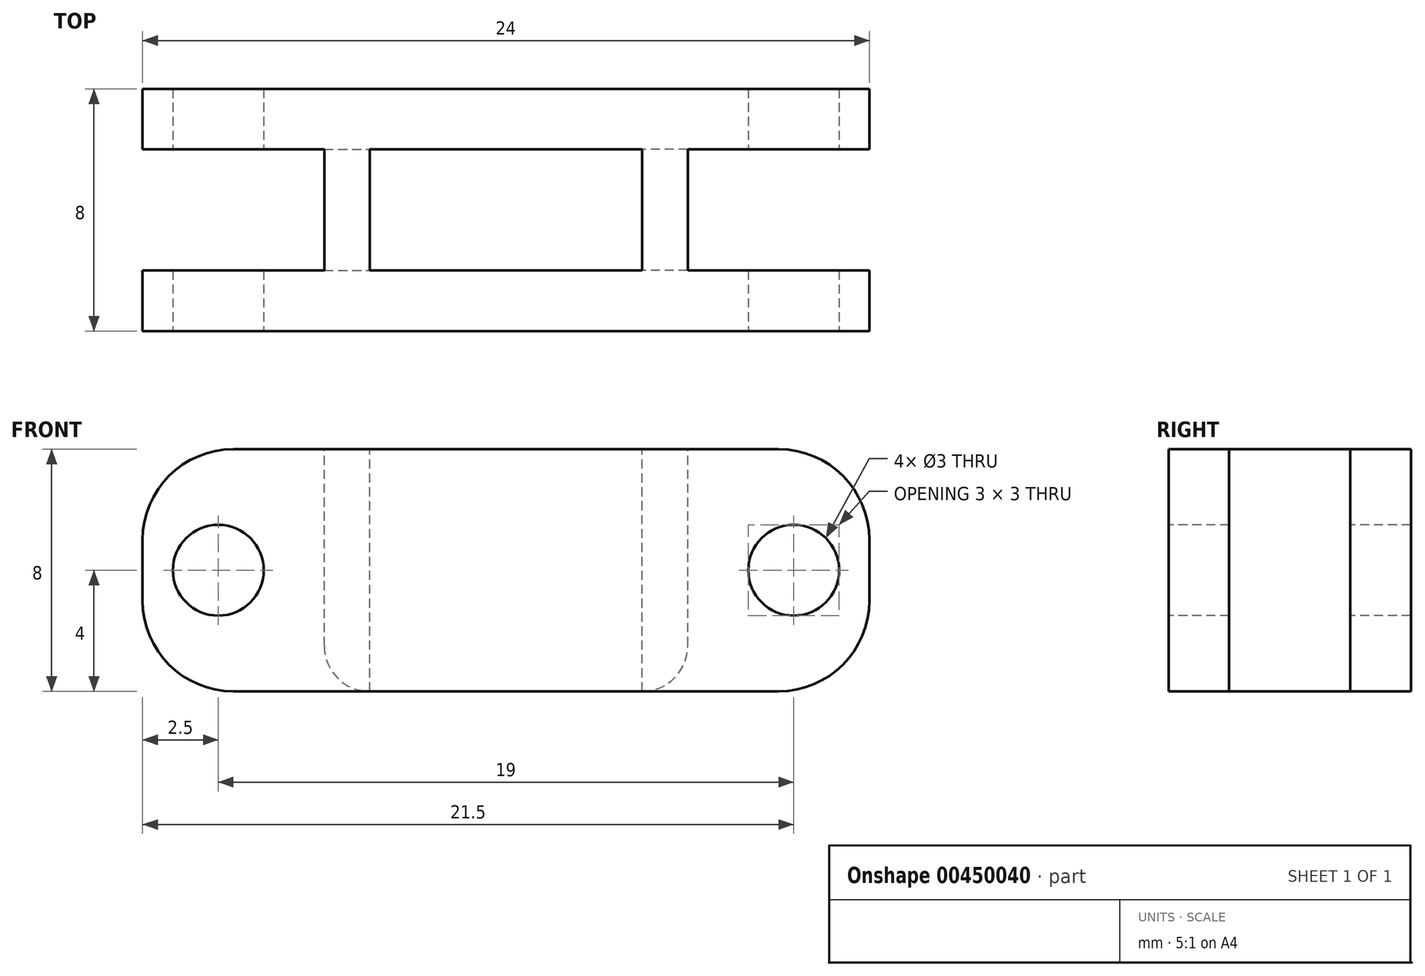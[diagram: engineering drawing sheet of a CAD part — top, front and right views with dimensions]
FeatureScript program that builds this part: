
annotation { "Feature Type Name" : "Feature", "Feature Type Description" : "" }
export const myFeature = defineFeature(function(context is Context, id is Id, definition is map)
    precondition{}
    {
        {
            var Q0;
            Q0=qCreatedBy(makeId("Top.planeOp"),FACE);
            var sketch = newSketch(context, id + "F0", { "sketchPlane" : qUnion([Q0])});
            skLineSegment(sketch, "E0.bottom", {"start": v(12, 4) * mm, "end": v(-12, 4) * mm});
            skLineSegment(sketch, "E0.top", {"start": v(12, -4) * mm, "end": v(-12, -4) * mm});
            skLineSegment(sketch, "E0.left", {"start": v(12, 4) * mm, "end": v(12, -4) * mm});
            skLineSegment(sketch, "E0.right", {"start": v(-12, 4) * mm, "end": v(-12, -4) * mm});
            skPoint(sketch, "E0.middle", {"position": v(0, 0) * mm});
            skSolve(sketch);
        }
        {
            var Q0;
            Q0 = qSketchRegion(id + "F0", true);
            extrude(context, id + "F1", {"entities" : qUnion([Q0]), "endBound" : BoundingType.SYMMETRIC, "depth" : 8 * mm});
        }
        {
            var Q0;
            Q0=makeQuery(id+"F1.opExtrude","CAP_FACE",FACE,{"disambiguationData":[OSD([sQuery(id+"F0.wireOp",EDGE,"E0.bottom"),sQuery(id+"F0.wireOp",EDGE,"E0.top"),sQuery(id+"F0.wireOp",EDGE,"E0.left"),sQuery(id+"F0.wireOp",EDGE,"E0.right")])],"isStart":false});
            var sketch = newSketch(context, id + "F2", { "sketchPlane" : qUnion([Q0])});
            skLineSegment(sketch, "E1.bottom", {"start": v(-12, 2) * mm, "end": v(-6, 2) * mm});
            skLineSegment(sketch, "E1.top", {"start": v(-12, -2) * mm, "end": v(-6, -2) * mm});
            skLineSegment(sketch, "E1.left", {"start": v(-12, 2) * mm, "end": v(-12, -2) * mm});
            skLineSegment(sketch, "E1.right", {"start": v(-6, 2) * mm, "end": v(-6, -2) * mm});
            skLineSegment(sketch, "E2.MirrorCS", {"start": v(6, 2) * mm, "end": v(6, -2) * mm});
            skLineSegment(sketch, "E3.MirrorCS", {"start": v(12, 2) * mm, "end": v(6, 2) * mm});
            skLineSegment(sketch, "E4.MirrorCS", {"start": v(12, 2) * mm, "end": v(12, -2) * mm});
            skLineSegment(sketch, "E5.MirrorCS", {"start": v(12, -2) * mm, "end": v(6, -2) * mm});
            skSolve(sketch);
        }
        {
            var Q0;
            Q0 = qSketchRegion(id + "F2", true);
            extrude(context, id + "F3", {"entities" : qUnion([Q0]), "operationType" : NewBodyOperationType.REMOVE, "oppositeDirection" : true, "depth" : 25 * mm});
        }
        {
            var Q0;
            Q0=makeQuery(id+"F1.opExtrude","SWEPT_FACE",FACE,{"disambiguationData":[OSD([sQuery(id+"F0.wireOp",EDGE,"E0.top")])]});
            var sketch = newSketch(context, id + "F4", { "sketchPlane" : qUnion([Q0])});
            skCircle(sketch, "E6", {"center": v(-9.5, 0) * mm, "radius": 1.5 * mm});
            skCircle(sketch, "E7.MirrorC", {"center": v(9.5, 0) * mm, "radius": 1.5 * mm});
            skSolve(sketch);
        }
        {
            var Q0;
            Q0 = qSketchRegion(id + "F4", true);
            extrude(context, id + "F5", {"entities" : qUnion([Q0]), "operationType" : NewBodyOperationType.REMOVE, "oppositeDirection" : true, "depth" : 25 * mm});
        }
        {
            var Q0;
            {var subQ0=sQuery(id+"F0.wireOp",EDGE,"E0.bottom");var subQ1=sQuery(id+"F0.wireOp",EDGE,"E0.left");Q0=makeQuery(id+"F3.boolean.opBoolean","SPLIT",EDGE,{"disambiguationData":[TD([makeQuery(id+"F1.opExtrude","SWEPT_FACE",FACE,{"disambiguationData":[OSD([subQ0])]})])],"derivedFrom":makeQuery(id+"F1.opExtrude","CAP_EDGE",EDGE,{"disambiguationData":[OSD([subQ1])],"isStart":false})});}
            var Q1;
            {var subQ0=sQuery(id+"F0.wireOp",EDGE,"E0.bottom");var subQ1=sQuery(id+"F0.wireOp",EDGE,"E0.left");Q1=makeQuery(id+"F3.boolean.opBoolean","SPLIT",EDGE,{"disambiguationData":[TD([makeQuery(id+"F1.opExtrude","SWEPT_FACE",FACE,{"disambiguationData":[OSD([subQ0])]})])],"derivedFrom":makeQuery(id+"F1.opExtrude","CAP_EDGE",EDGE,{"disambiguationData":[OSD([subQ1])],"isStart":true})});}
            var Q2;
            {var subQ0=sQuery(id+"F0.wireOp",EDGE,"E0.left");var subQ1=sQuery(id+"F0.wireOp",EDGE,"E0.top");Q2=makeQuery(id+"F3.boolean.opBoolean","SPLIT",EDGE,{"disambiguationData":[TD([makeQuery(id+"F1.opExtrude","SWEPT_FACE",FACE,{"disambiguationData":[OSD([subQ1])]})])],"derivedFrom":makeQuery(id+"F1.opExtrude","CAP_EDGE",EDGE,{"disambiguationData":[OSD([subQ0])],"isStart":true})});}
            var Q3;
            {var subQ0=sQuery(id+"F0.wireOp",EDGE,"E0.right");var subQ1=sQuery(id+"F0.wireOp",EDGE,"E0.top");Q3=makeQuery(id+"F3.boolean.opBoolean","SPLIT",EDGE,{"disambiguationData":[TD([makeQuery(id+"F1.opExtrude","SWEPT_FACE",FACE,{"disambiguationData":[OSD([subQ1])]})])],"derivedFrom":makeQuery(id+"F1.opExtrude","CAP_EDGE",EDGE,{"disambiguationData":[OSD([subQ0])],"isStart":false})});}
            var Q4;
            {var subQ0=sQuery(id+"F0.wireOp",EDGE,"E0.bottom");var subQ1=sQuery(id+"F0.wireOp",EDGE,"E0.right");Q4=makeQuery(id+"F3.boolean.opBoolean","SPLIT",EDGE,{"disambiguationData":[TD([makeQuery(id+"F1.opExtrude","SWEPT_FACE",FACE,{"disambiguationData":[OSD([subQ0])]})])],"derivedFrom":makeQuery(id+"F1.opExtrude","CAP_EDGE",EDGE,{"disambiguationData":[OSD([subQ1])],"isStart":false})});}
            var Q5;
            {var subQ0=sQuery(id+"F0.wireOp",EDGE,"E0.right");var subQ1=sQuery(id+"F0.wireOp",EDGE,"E0.top");Q5=makeQuery(id+"F3.boolean.opBoolean","SPLIT",EDGE,{"disambiguationData":[TD([makeQuery(id+"F1.opExtrude","SWEPT_FACE",FACE,{"disambiguationData":[OSD([subQ1])]})])],"derivedFrom":makeQuery(id+"F1.opExtrude","CAP_EDGE",EDGE,{"disambiguationData":[OSD([subQ0])],"isStart":true})});}
            var Q6;
            {var subQ0=sQuery(id+"F0.wireOp",EDGE,"E0.bottom");var subQ1=sQuery(id+"F0.wireOp",EDGE,"E0.right");Q6=makeQuery(id+"F3.boolean.opBoolean","SPLIT",EDGE,{"disambiguationData":[TD([makeQuery(id+"F1.opExtrude","SWEPT_FACE",FACE,{"disambiguationData":[OSD([subQ0])]})])],"derivedFrom":makeQuery(id+"F1.opExtrude","CAP_EDGE",EDGE,{"disambiguationData":[OSD([subQ1])],"isStart":true})});}
            var Q7;
            {var subQ0=sQuery(id+"F0.wireOp",EDGE,"E0.left");var subQ1=sQuery(id+"F0.wireOp",EDGE,"E0.top");Q7=makeQuery(id+"F3.boolean.opBoolean","SPLIT",EDGE,{"disambiguationData":[TD([makeQuery(id+"F1.opExtrude","SWEPT_FACE",FACE,{"disambiguationData":[OSD([subQ1])]})])],"derivedFrom":makeQuery(id+"F1.opExtrude","CAP_EDGE",EDGE,{"disambiguationData":[OSD([subQ0])],"isStart":false})});}
            fillet(context, id + "F6", {"entities" : qUnion([Q0, Q1, Q2, Q3, Q4, Q5, Q6, Q7]), "radius" : 3 * mm, "tangentPropagation" : true, "allowEdgeOverflow" : false});
        }
        {
            var Q0;
            Q0=makeQuery(id+"F3.boolean.opBoolean","COPY",EDGE,{"derivedFrom":makeQuery(id+"F3.opExtrude","CAP_EDGE",EDGE,{"disambiguationData":[OSD([sQuery(id+"F2.wireOp",EDGE,"E2.MirrorCS")])],"isStart":true})});
            var Q1;
            Q1=makeQuery(id+"F3.boolean.opBoolean","COPY",EDGE,{"derivedFrom":makeQuery(id+"F3.opExtrude","CAP_EDGE",EDGE,{"disambiguationData":[OSD([sQuery(id+"F2.wireOp",EDGE,"E1.right")])],"isStart":true})});
            var Q2;
            Q2=makeQuery(id+"F3.boolean.opBoolean","INTERSECT",EDGE,{"derivedFrom":[makeQuery(id+"F1.opExtrude","CAP_FACE",FACE,{"disambiguationData":[OSD([sQuery(id+"F0.wireOp",EDGE,"E0.bottom"),sQuery(id+"F0.wireOp",EDGE,"E0.top"),sQuery(id+"F0.wireOp",EDGE,"E0.left"),sQuery(id+"F0.wireOp",EDGE,"E0.right")])],"isStart":true}),makeQuery(id+"F3.opExtrude","SWEPT_FACE",FACE,{"disambiguationData":[OSD([sQuery(id+"F2.wireOp",EDGE,"E2.MirrorCS")])]})]});
            var Q3;
            Q3=makeQuery(id+"F3.boolean.opBoolean","INTERSECT",EDGE,{"derivedFrom":[makeQuery(id+"F1.opExtrude","CAP_FACE",FACE,{"disambiguationData":[OSD([sQuery(id+"F0.wireOp",EDGE,"E0.bottom"),sQuery(id+"F0.wireOp",EDGE,"E0.top"),sQuery(id+"F0.wireOp",EDGE,"E0.left"),sQuery(id+"F0.wireOp",EDGE,"E0.right")])],"isStart":true}),makeQuery(id+"F3.opExtrude","SWEPT_FACE",FACE,{"disambiguationData":[OSD([sQuery(id+"F2.wireOp",EDGE,"E1.right")])]})]});
            fillet(context, id + "F7", {"entities" : qUnion([Q0, Q1, Q2, Q3]), "radius" : 1.5 * mm, "tangentPropagation" : true, "allowEdgeOverflow" : false});
        }
        {
            var Q0;
            Q0=makeQuery(id+"F1.opExtrude","CAP_FACE",FACE,{"disambiguationData":[OSD([sQuery(id+"F0.wireOp",EDGE,"E0.bottom"),sQuery(id+"F0.wireOp",EDGE,"E0.top"),sQuery(id+"F0.wireOp",EDGE,"E0.left"),sQuery(id+"F0.wireOp",EDGE,"E0.right")])],"isStart":false});
            var sketch = newSketch(context, id + "F8", { "sketchPlane" : qUnion([Q0])});
            skLineSegment(sketch, "E8.bottom", {"start": v(-4.5, 2) * mm, "end": v(4.5, 2) * mm});
            skLineSegment(sketch, "E8.top", {"start": v(-4.5, -2) * mm, "end": v(4.5, -2) * mm});
            skLineSegment(sketch, "E8.left", {"start": v(-4.5, 2) * mm, "end": v(-4.5, -2) * mm});
            skLineSegment(sketch, "E8.right", {"start": v(4.5, 2) * mm, "end": v(4.5, -2) * mm});
            skSolve(sketch);
        }
        {
            var Q0;
            Q0 = qSketchRegion(id + "F8", true);
            extrude(context, id + "F9", {"entities" : qUnion([Q0]), "operationType" : NewBodyOperationType.REMOVE, "oppositeDirection" : true, "depth" : 25 * mm});
        }
    });
